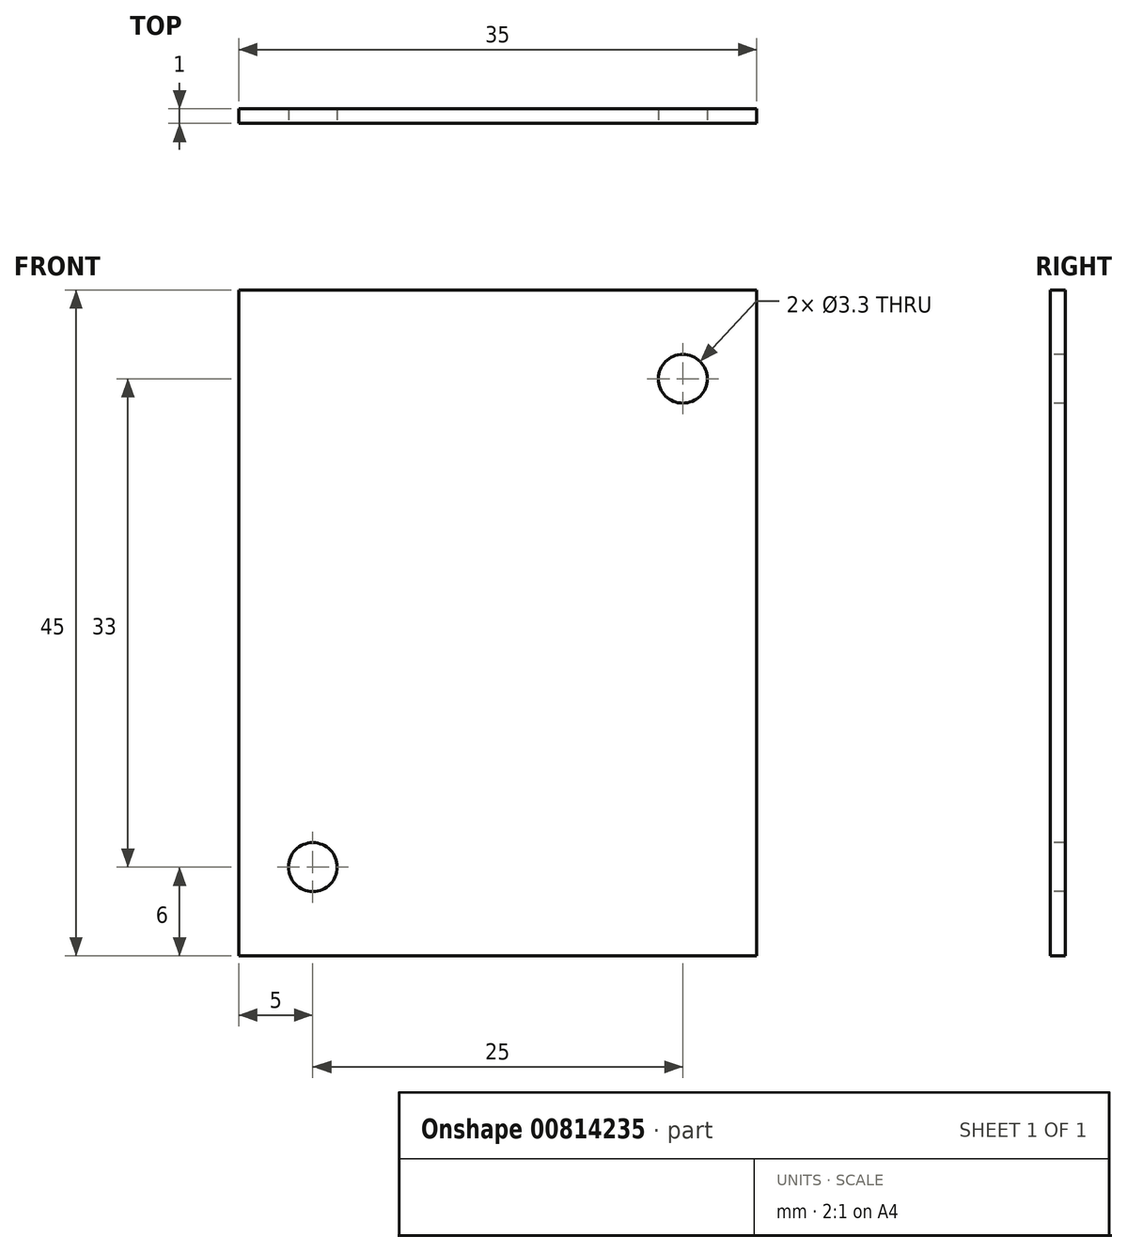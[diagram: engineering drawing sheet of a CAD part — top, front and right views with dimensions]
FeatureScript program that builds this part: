
annotation { "Feature Type Name" : "Feature", "Feature Type Description" : "" }
export const myFeature = defineFeature(function(context is Context, id is Id, definition is map)
    precondition{}
    {
        {
            var Q0;
            Q0=qCreatedBy(makeId("Front.planeOp"),FACE);
            var sketch = newSketch(context, id + "F0", { "sketchPlane" : qUnion([Q0])});
            skLineSegment(sketch, "E0.bottom", {"start": v(0, 0) * mm, "end": v(35, 0) * mm});
            skLineSegment(sketch, "E0.top", {"start": v(0, 45) * mm, "end": v(35, 45) * mm});
            skLineSegment(sketch, "E0.left", {"start": v(0, 0) * mm, "end": v(0, 45) * mm});
            skLineSegment(sketch, "E0.right", {"start": v(35, 0) * mm, "end": v(35, 45) * mm});
            skSolve(sketch);
        }
        {
            var Q0;
            Q0=makeQuery(id+"F0.imprint","IMPRINT",FACE,{"disambiguationData":[TD([[makeQuery(id+"F0.imprint","IMPRINT",EDGE,{"derivedFrom":sQuery(id+"F0.wireOp",EDGE,"E0.bottom")}),1.0]])]});
            extrude(context, id + "F1", {"entities" : qUnion([Q0]), "depth" : 1 * mm, "offsetDistance" : 25 * mm});
        }
        {
            var Q0;
            Q0=makeQuery(id+"F1.opExtrude","CAP_FACE",FACE,{"disambiguationData":[OSD([sQuery(id+"F0.wireOp",EDGE,"E0.bottom"),sQuery(id+"F0.wireOp",EDGE,"E0.top"),sQuery(id+"F0.wireOp",EDGE,"E0.left"),sQuery(id+"F0.wireOp",EDGE,"E0.right")])],"isStart":false});
            var sketch = newSketch(context, id + "F2", { "sketchPlane" : qUnion([Q0])});
            skPoint(sketch, "E1", {"position": v(30, 39) * mm});
            skPoint(sketch, "E2", {"position": v(5, 6) * mm});
            skSolve(sketch);
        }
        {
            var Q0;
            Q0=sQuery(id+"F2.wireOp",VERTEX,"E1");
            var Q1;
            Q1=sQuery(id+"F2.wireOp",VERTEX,"E2");
            var Q2;
            Q2=makeQuery(id+"F1.opExtrude","SWEPT_BODY",BODY,{"disambiguationData":[OSD([sQuery(id+"F0.wireOp",EDGE,"E0.bottom"),sQuery(id+"F0.wireOp",EDGE,"E0.top"),sQuery(id+"F0.wireOp",EDGE,"E0.left"),sQuery(id+"F0.wireOp",EDGE,"E0.right")])]});
            hole(context, id + "F3", {"style" : HoleStyle.SIMPLE, "endStyle" : HoleEndStyle.THROUGH, "standardTappedOrClearance" : lookupTablePath({ "standard" : "ISO", "fit" : "Normal", "size" : "M3", "type" : "Clearance" }), "standardBlindInLast" : lookupTablePath({ "fit" : "Standard", "standard" : "ISO", "size" : "M3", "type" : "Clearance" }), "holeDiameter" : 3.3 * mm, "majorDiameter" : 8 * mm, "isTappedThrough" : true, "tappedDepth" : 18.25 * mm, "tapClearance" : 3, "locations" : qUnion([Q0, Q1]), "scope" : qUnion([Q2])});
        }
    });
